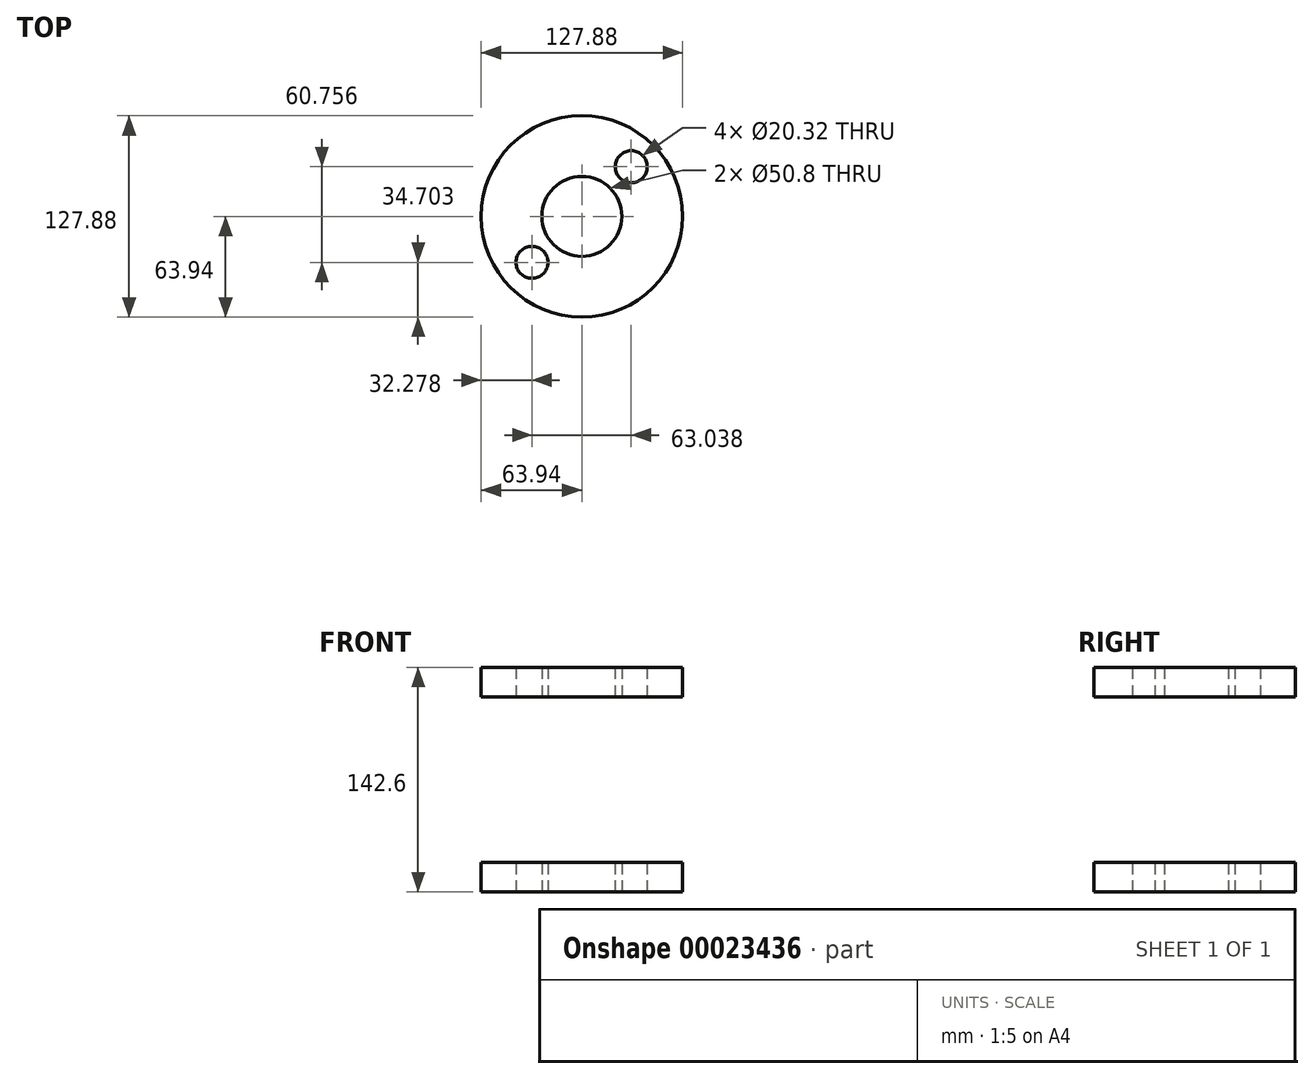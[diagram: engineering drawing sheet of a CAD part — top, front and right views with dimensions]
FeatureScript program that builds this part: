
annotation { "Feature Type Name" : "Feature", "Feature Type Description" : "" }
export const myFeature = defineFeature(function(context is Context, id is Id, definition is map)
    precondition{}
    {
        {
            var Q0;
            Q0=qCreatedBy(makeId("Top.planeOp"),FACE);
            var sketch = newSketch(context, id + "F0", { "sketchPlane" : qUnion([Q0])});
            skCircle(sketch, "E0", {"center": v(0, 0) * mm, "radius": 63.94 * mm});
            skSolve(sketch);
        }
        {
            var Q0;
            Q0=makeQuery(id+"F0.imprint","IMPRINT",FACE,{"disambiguationData":[TD([[makeQuery(id+"F0.imprint","IMPRINT",EDGE,{"derivedFrom":sQuery(id+"F0.wireOp",EDGE,"E0")}),1.0]])]});
            var sketch = newSketch(context, id + "F1", { "sketchPlane" : qUnion([Q0])});
            skCircle(sketch, "E1", {"center": v(0, 0) * mm, "radius": 25.4 * mm});
            skCircle(sketch, "E2", {"center": v(31.38, 31.52) * mm, "radius": 10.16 * mm});
            skCircle(sketch, "E3", {"center": v(-31.66, -29.24) * mm, "radius": 10.16 * mm});
            skSolve(sketch);
        }
        {
            var Q0;
            Q0=makeQuery(id+"F1.imprint","IMPRINT",FACE,{"disambiguationData":[TD([[makeQuery(id+"F1.imprint","IMPRINT",EDGE,{"derivedFrom":sQuery(id+"F1.wireOp",EDGE,"E1")}),-1.0]])]});
            extrude(context, id + "F2", {"entities" : qUnion([Q0]), "endBound" : BoundingType.SYMMETRIC, "depth" : 142.6 * mm});
        }
        {
            var Q0;
            Q0=qCreatedBy(makeId("Top.planeOp"),FACE);
            var sketch = newSketch(context, id + "F3", { "sketchPlane" : qUnion([Q0])});
            skCircle(sketch, "E4", {"center": v(0, 0) * mm, "radius": 73 * mm});
            skSolve(sketch);
        }
        {
            var Q0;
            Q0 = qSketchRegion(id + "F3", true);
            extrude(context, id + "F4", {"entities" : qUnion([Q0]), "operationType" : NewBodyOperationType.REMOVE, "endBound" : BoundingType.SYMMETRIC, "oppositeDirection" : true, "depth" : 105.19 * mm});
        }
        {
            var Q0;
            Q0=qCreatedBy(makeId("Top.planeOp"),FACE);
            var sketch = newSketch(context, id + "F5", { "sketchPlane" : qUnion([Q0])});
            skCircle(sketch, "E5", {"center": v(-39.36, 44.07) * mm, "radius": 3.18 * mm});
            skCircle(sketch, "E6", {"center": v(42.22, -32.66) * mm, "radius": 3.18 * mm});
            skSolve(sketch);
        }
        {
            var Q0;
            Q0=sQuery(id+"F5.wireOp",EDGE,"E6");
            extrude(context, id + "F6", {"bodyType" : ToolBodyType.SURFACE, "surfaceEntities" : qUnion([Q0]), "endBound" : BoundingType.SYMMETRIC, "depth" : 111.27 * mm});
        }
        {
            var Q0;
            Q0=qCreatedBy(makeId("Top.planeOp"),FACE);
            var sketch = newSketch(context, id + "F7", { "sketchPlane" : qUnion([Q0])});
            skCircle(sketch, "E7", {"center": v(-39.36, 39.5) * mm, "radius": 3.18 * mm});
            skSolve(sketch);
        }
        {
            var Q0;
            Q0=sQuery(id+"F7.wireOp",EDGE,"E7");
            extrude(context, id + "F8", {"bodyType" : ToolBodyType.SURFACE, "surfaceEntities" : qUnion([Q0]), "endBound" : BoundingType.SYMMETRIC, "depth" : 141.13 * mm});
        }
    });
